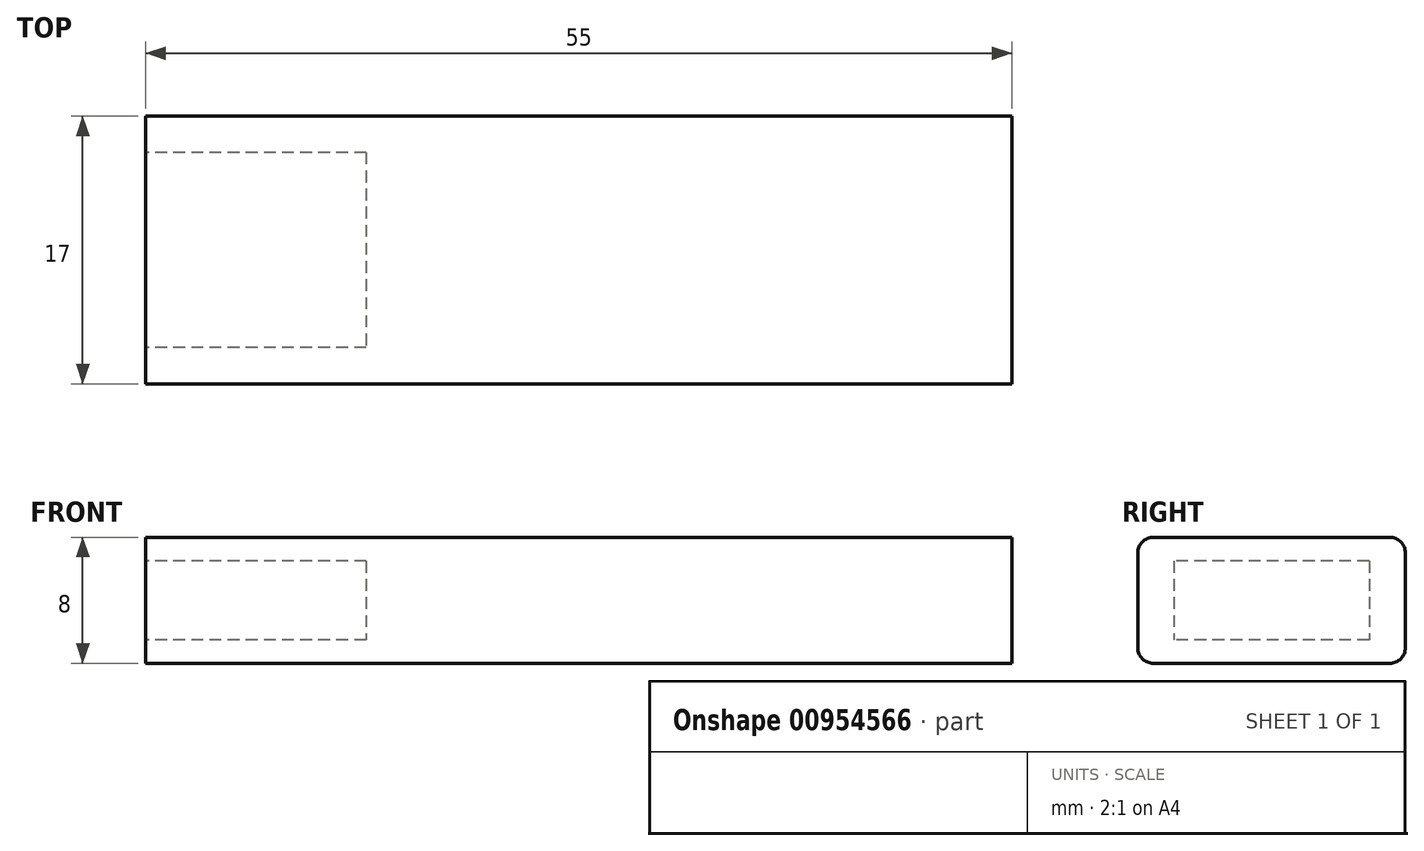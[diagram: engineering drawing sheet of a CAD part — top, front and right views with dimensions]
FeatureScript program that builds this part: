
annotation { "Feature Type Name" : "Feature", "Feature Type Description" : "" }
export const myFeature = defineFeature(function(context is Context, id is Id, definition is map)
    precondition{}
    {
        {
            var Q0;
            Q0=qCreatedBy(makeId("Front.planeOp"),FACE);
            var sketch = newSketch(context, id + "F0", { "sketchPlane" : qUnion([Q0])});
            skLineSegment(sketch, "E0.bottom", {"start": v(76.77, 74) * mm, "end": v(-76.77, 74) * mm});
            skLineSegment(sketch, "E0.top", {"start": v(76.77, -74) * mm, "end": v(-76.77, -74) * mm});
            skLineSegment(sketch, "E0.left", {"start": v(76.77, 74) * mm, "end": v(76.77, -74) * mm});
            skLineSegment(sketch, "E0.right", {"start": v(-76.77, 74) * mm, "end": v(-76.77, -74) * mm});
            skPoint(sketch, "E0.middle", {"position": v(0, 0) * mm});
            skSolve(sketch);
        }
        {
            var Q0;
            Q0=makeQuery(id+"F0.imprint","IMPRINT",FACE,{"disambiguationData":[TD([[makeQuery(id+"F0.imprint","IMPRINT",EDGE,{"derivedFrom":sQuery(id+"F0.wireOp",EDGE,"E0.bottom")}),1.0]])]});
            var sketch = newSketch(context, id + "F1", { "sketchPlane" : qUnion([Q0])});
            skLineSegment(sketch, "E1.bottom", {"start": v(-7.5, 4) * mm, "end": v(7.5, 4) * mm});
            skLineSegment(sketch, "E1.top", {"start": v(-7.5, -4) * mm, "end": v(7.5, -4) * mm});
            skLineSegment(sketch, "E1.left", {"start": v(-8.5, 3) * mm, "end": v(-8.5, -3) * mm});
            skLineSegment(sketch, "E1.right", {"start": v(8.5, 3) * mm, "end": v(8.5, -3) * mm});
            skPoint(sketch, "E1.middle", {"position": v(0, 0) * mm});
            skPoint(sketch, "E2.visualSharp", {"position": v(-8.5, 4) * mm});
            skArc(sketch, "E2.filletArc", {"start": v(-7.5, 4) * mm, "mid": v(-8.2, 3.7) * mm, "end": v(-8.5, 3) * mm});
            skPoint(sketch, "E3.visualSharp", {"position": v(-8.5, -4) * mm});
            skArc(sketch, "E3.filletArc", {"start": v(-8.5, -3) * mm, "mid": v(-8.2, -3.7) * mm, "end": v(-7.5, -4) * mm});
            skPoint(sketch, "E4.visualSharp", {"position": v(8.5, 4) * mm});
            skArc(sketch, "E4.filletArc", {"start": v(8.5, 3) * mm, "mid": v(8.2, 3.7) * mm, "end": v(7.5, 4) * mm});
            skPoint(sketch, "E5.visualSharp", {"position": v(8.5, -4) * mm});
            skArc(sketch, "E5.filletArc", {"start": v(7.5, -4) * mm, "mid": v(8.2, -3.7) * mm, "end": v(8.5, -3) * mm});
            skSolve(sketch);
        }
        {
            var Q0;
            Q0 = qSketchRegion(id + "F1", true);
            extrude(context, id + "F2", {"entities" : qUnion([Q0]), "depth" : 55 * mm, "offsetDistance" : 25 * mm});
        }
        {
            var Q0;
            Q0=makeQuery(id+"F2.opExtrude","CAP_FACE",FACE,{"disambiguationData":[OSD([sQuery(id+"F1.wireOp",EDGE,"E1.bottom"),sQuery(id+"F1.wireOp",EDGE,"E1.top"),sQuery(id+"F1.wireOp",EDGE,"E1.left"),sQuery(id+"F1.wireOp",EDGE,"E1.right"),sQuery(id+"F1.wireOp",EDGE,"E2.filletArc"),sQuery(id+"F1.wireOp",EDGE,"E3.filletArc"),sQuery(id+"F1.wireOp",EDGE,"E4.filletArc"),sQuery(id+"F1.wireOp",EDGE,"E5.filletArc")])],"isStart":false});
            var sketch = newSketch(context, id + "F3", { "sketchPlane" : qUnion([Q0])});
            skLineSegment(sketch, "E6.bottom", {"start": v(-6.2, 2.5) * mm, "end": v(6.2, 2.5) * mm});
            skLineSegment(sketch, "E6.top", {"start": v(-6.2, -2.5) * mm, "end": v(6.2, -2.5) * mm});
            skLineSegment(sketch, "E6.left", {"start": v(-6.2, 2.5) * mm, "end": v(-6.2, -2.5) * mm});
            skLineSegment(sketch, "E6.right", {"start": v(6.2, 2.5) * mm, "end": v(6.2, -2.5) * mm});
            skPoint(sketch, "E6.middle", {"position": v(0, 0) * mm});
            skSolve(sketch);
        }
        {
            var Q0;
            Q0=makeQuery(id+"F3.imprint","IMPRINT",FACE,{"disambiguationData":[TD([[makeQuery(id+"F3.imprint","IMPRINT",EDGE,{"derivedFrom":sQuery(id+"F3.wireOp",EDGE,"E6.bottom")}),-1.0]])]});
            extrude(context, id + "F4", {"entities" : qUnion([Q0]), "operationType" : NewBodyOperationType.REMOVE, "oppositeDirection" : true, "depth" : 14 * mm, "offsetDistance" : 25 * mm});
        }
        {
            var Q0;
            Q0=makeQuery(id+"F2.opExtrude","SWEPT_FACE",FACE,{"disambiguationData":[OSD([sQuery(id+"F1.wireOp",EDGE,"E1.bottom")])]});
            var sketch = newSketch(context, id + "F5", { "sketchPlane" : qUnion([Q0])});
            skSolve(sketch);
        }
        {
            var Q0;
            Q0=makeQuery(id+"F2.opExtrude","SWEPT_BODY",BODY,{"disambiguationData":[OSD([sQuery(id+"F1.wireOp",EDGE,"E1.bottom"),sQuery(id+"F1.wireOp",EDGE,"E1.top"),sQuery(id+"F1.wireOp",EDGE,"E1.left"),sQuery(id+"F1.wireOp",EDGE,"E1.right"),sQuery(id+"F1.wireOp",EDGE,"E2.filletArc"),sQuery(id+"F1.wireOp",EDGE,"E3.filletArc"),sQuery(id+"F1.wireOp",EDGE,"E4.filletArc"),sQuery(id+"F1.wireOp",EDGE,"E5.filletArc")])]});
            var Q1;
            Q1=makeQuery(id+"F2.opExtrude","CAP_EDGE",EDGE,{"disambiguationData":[OSD([sQuery(id+"F1.wireOp",EDGE,"E1.left")])],"isStart":false});
            transform(context, id + "F6", {"entities" : qUnion([Q0]), "transformType" : TransformType.ROTATION, "transformAxis" : qUnion([Q1]), "angle" : 90 * degree, "makeCopy" : false});
        }
    });
